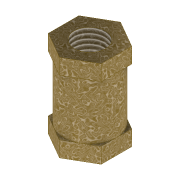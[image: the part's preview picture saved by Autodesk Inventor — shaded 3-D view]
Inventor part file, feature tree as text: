
AUTODESK INVENTOR PART (.ipt)
format: ipt  version: 2021 (Build 250183000, 183)  size: 129,024 bytes
history: native  units: mm
features: extrude x2, sketch x2, thread x1
ambient origin geometry x8: Origin, YZ Plane, XZ Plane, XY Plane, X Axis, Y Axis, Z Axis, Center Point
bodies: Solid1 (feature_tree)
feature tree (5):
  extrude  "Extrusion1"  Depth=10.0mm
  extrude  "Extrusion2"  Depth=17.0mm
  thread  "Thread1"  [1 undecoded]
  sketch  "Sketch1"  dims[d0=17.0mm d1=10.0mm]
  sketch  "Sketch2"  dims[d2=28.0mm d3=0.0mm d4=17.0mm d5=34.0mm d6=-18.0mm d7=0.0mm d8=28.0mm d9=0.0mm]
note: 1 required parameter value undecoded (feature->parameter linkage not recoverable at this tier; creation-order binding heuristic only, values carry confidence <= 0.55)
